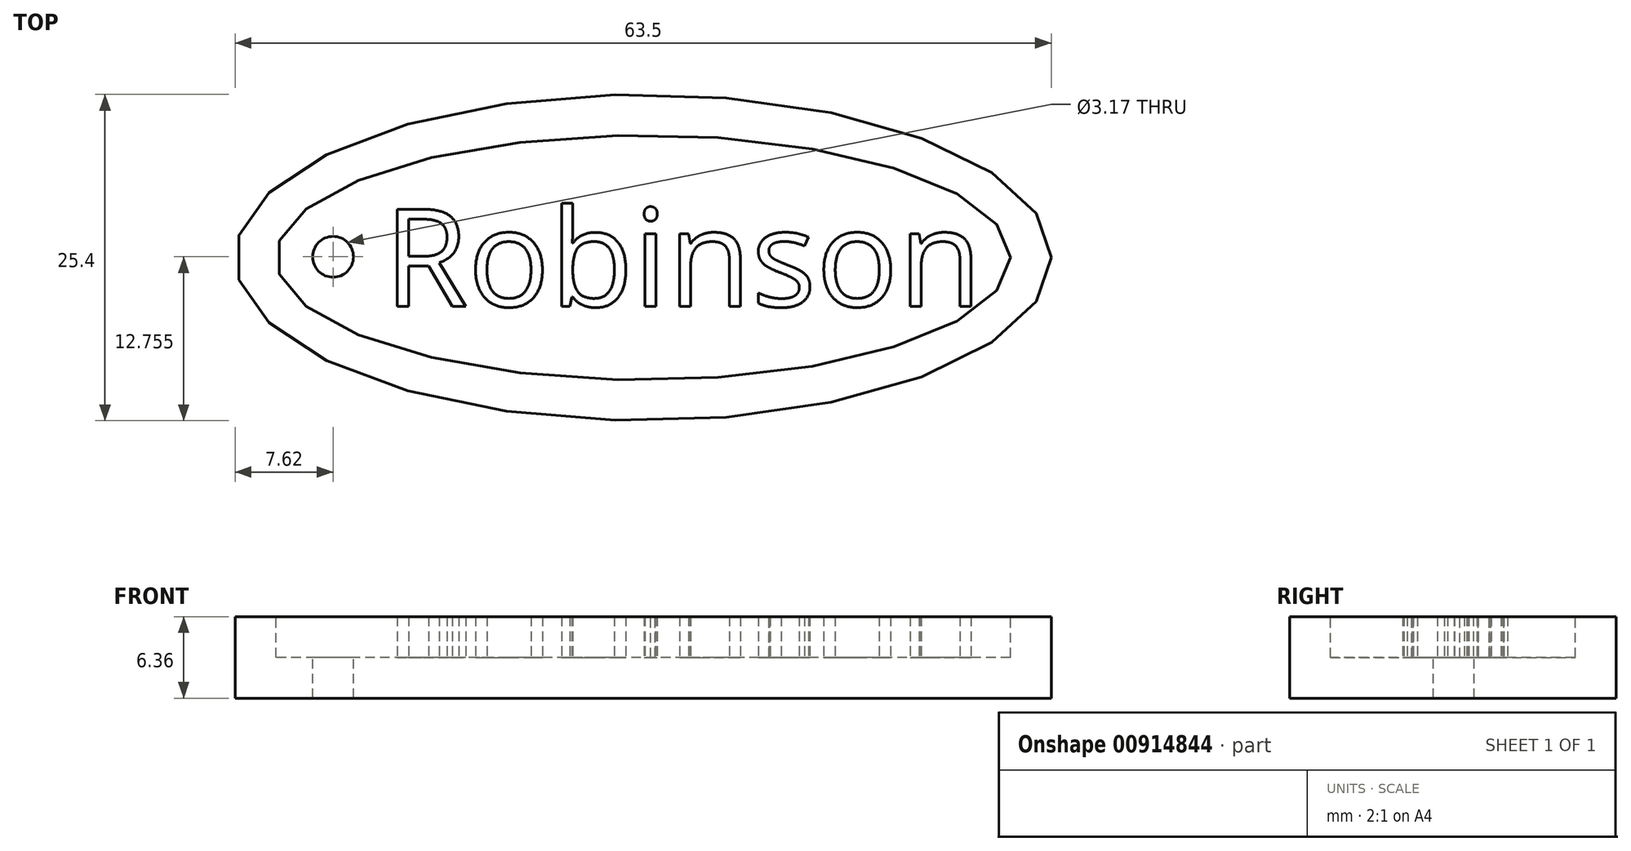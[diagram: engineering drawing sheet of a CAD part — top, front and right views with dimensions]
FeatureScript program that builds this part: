
annotation { "Feature Type Name" : "Feature", "Feature Type Description" : "" }
export const myFeature = defineFeature(function(context is Context, id is Id, definition is map)
    precondition{}
    {
        {
            var Q0;
            Q0=qCreatedBy(makeId("Top.planeOp"),FACE);
            var sketch = newSketch(context, id + "F0", { "sketchPlane" : qUnion([Q0])});
            skEllipse(sketch, "E0", {"center": v(0, 0) * mm, "majorRadius": 31.75 * mm, "minorRadius": 12.7 * mm, "majorAxis": v(1, 0)});
            skSolve(sketch);
        }
        {
            var Q0;
            Q0=makeQuery(id+"F0.imprint","IMPRINT",FACE,{"disambiguationData":[TD([[makeQuery(id+"F0.imprint","IMPRINT",EDGE,{"derivedFrom":sQuery(id+"F0.wireOp",EDGE,"E0")}),1.0]])]});
            extrude(context, id + "F1", {"entities" : qUnion([Q0]), "endBound" : BoundingType.SYMMETRIC, "depth" : 6.35 * mm, "offsetDistance" : 25.4 * mm});
        }
        {
            var Q0;
            Q0=makeQuery(id+"F1.opExtrude","CAP_FACE",FACE,{"disambiguationData":[OSD([sQuery(id+"F0.wireOp",EDGE,"E0")])],"isStart":false});
            var sketch = newSketch(context, id + "F2", { "sketchPlane" : qUnion([Q0])});
            skEllipse(sketch, "E1", {"center": v(0, 0) * mm, "majorRadius": 28.58 * mm, "minorRadius": 9.53 * mm, "majorAxis": v(1, 0)});
            skSolve(sketch);
        }
        {
            var Q0;
            Q0=qSketchRegion(id+"F2",true);
            var Q1;
            Q1 = qSketchRegion(id + "F4", true);
            extrude(context, id + "F3", {"entities" : qUnion([Q0, Q1]), "operationType" : NewBodyOperationType.REMOVE, "oppositeDirection" : true, "depth" : 3.17 * mm, "offsetDistance" : 25.4 * mm});
        }
        {
            var Q0;
            Q0=makeQuery(id+"F3.boolean.opBoolean","COPY",FACE,{"derivedFrom":makeQuery(id+"F3.opExtrude","CAP_FACE",FACE,{"disambiguationData":[OSD([sQuery(id+"F2.wireOp",EDGE,"E1")])],"isStart":false})});
            var sketch = newSketch(context, id + "F4", { "sketchPlane" : qUnion([Q0])});
            skText(sketch, "E2", { "text": "Robinson ", "fontName": "OpenSans-Regular.ttf"});
            const initialGuessF4  = {"E2": [-0.02018, -0.0038, 1, 0, 0.00762]};
            skSetInitialGuess(sketch, initialGuessF4);
            skSolve(sketch);
        }
        {
            var Q0;
            Q0 = qSketchRegion(id + "F4", true);
            extrude(context, id + "F5", {"entities" : qUnion([Q0]), "operationType" : NewBodyOperationType.ADD, "depth" : 3.17 * mm, "offsetDistance" : 25.4 * mm});
        }
        {
            var Q0;
            Q0=makeQuery(id+"F4.imprint","IMPRINT",FACE,{"disambiguationData":[TD([[makeQuery(id+"F4.imprint","IMPRINT",EDGE,{"derivedFrom":makeQuery(id+"F3.boolean.opBoolean","COPY",EDGE,{"derivedFrom":makeQuery(id+"F3.opExtrude","CAP_EDGE",EDGE,{"disambiguationData":[OSD([sQuery(id+"F2.wireOp",EDGE,"E1")])],"isStart":false})})}),1.0]])]});
            var sketch = newSketch(context, id + "F6", { "sketchPlane" : qUnion([Q0])});
            skCircle(sketch, "E3", {"center": v(-24.13, 0.05) * mm, "radius": 1.59 * mm});
            skSolve(sketch);
        }
        {
            var Q0;
            Q0=qSketchRegion(id+"F6",true);
            extrude(context, id + "F7", {"entities" : qUnion([Q0]), "operationType" : NewBodyOperationType.REMOVE, "endBound" : BoundingType.THROUGH_ALL, "oppositeDirection" : true, "depth" : 25.4 * mm, "offsetDistance" : 25.4 * mm});
        }
    });
